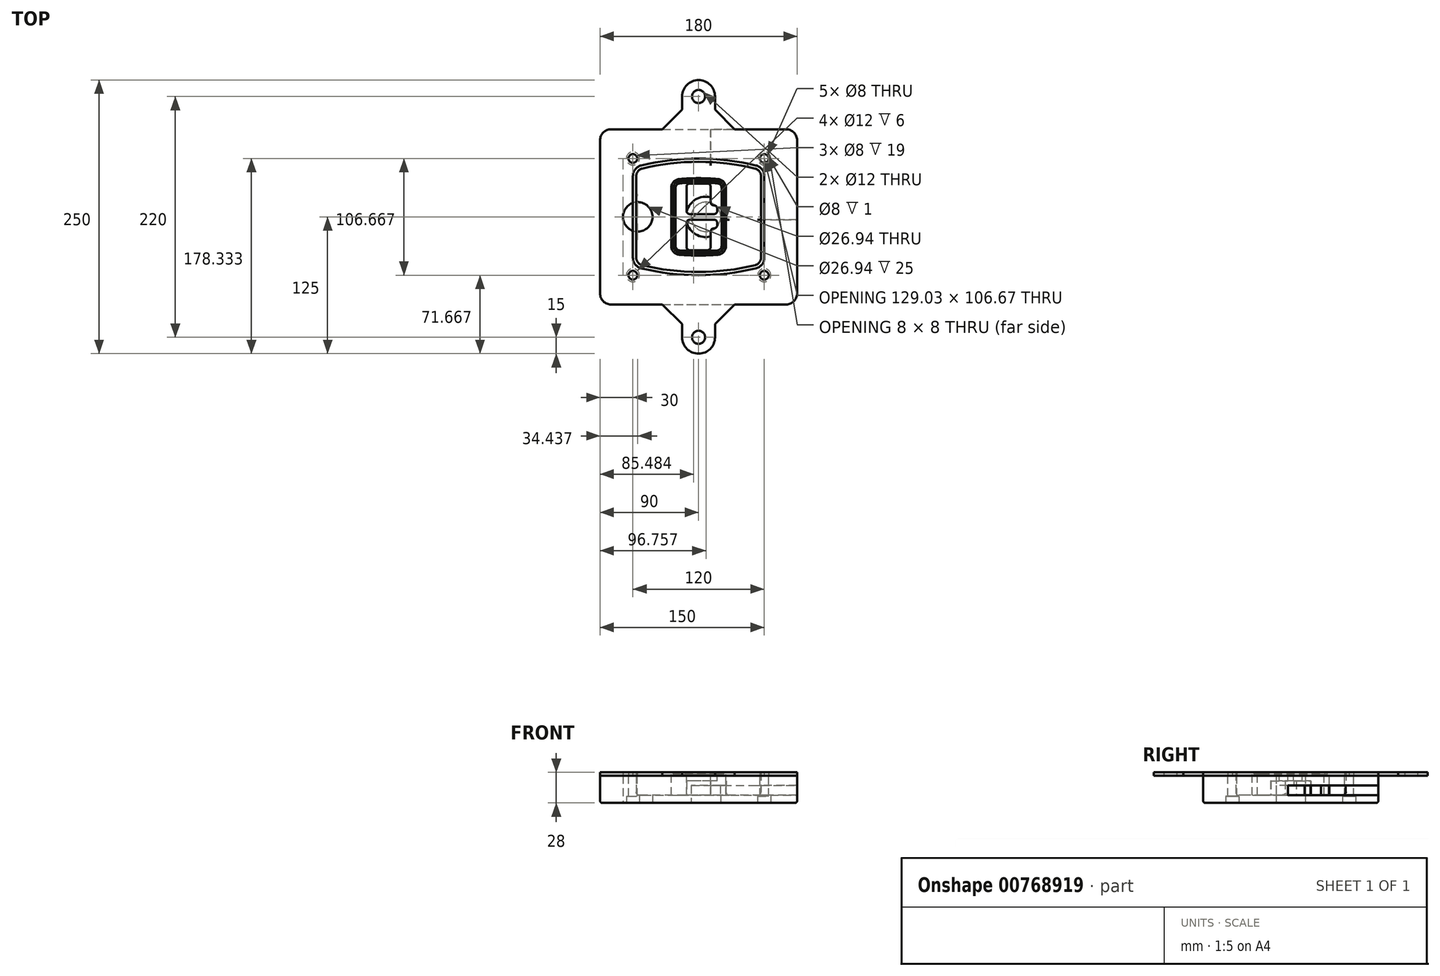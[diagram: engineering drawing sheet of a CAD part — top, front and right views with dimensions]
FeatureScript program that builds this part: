
annotation { "Feature Type Name" : "Feature", "Feature Type Description" : "" }
export const myFeature = defineFeature(function(context is Context, id is Id, definition is map)
    precondition{}
    {
        {
            var Q0;
            Q0=qCreatedBy(makeId("Top.planeOp"),FACE);
            var sketch = newSketch(context, id + "F0", { "sketchPlane" : qUnion([Q0])});
            skPoint(sketch, "E0.rect.middle", {"position": v(0, 0) * mm});
            skLineSegment(sketch, "E1.bottom", {"start": v(-80, -80) * mm, "end": v(80, -80) * mm});
            skLineSegment(sketch, "E1.top", {"start": v(-80, 80) * mm, "end": v(80, 80) * mm});
            skLineSegment(sketch, "E1.left", {"start": v(-90, -70) * mm, "end": v(-90, 70) * mm});
            skLineSegment(sketch, "E1.right", {"start": v(90, -70) * mm, "end": v(90, 70) * mm});
            skLineSegment(sketch, "E2", {"start": v(-90, 80) * mm, "end": v(90, -80) * mm, "construction": true});
            skLineSegment(sketch, "E3", {"start": v(90, 80) * mm, "end": v(-90, -80) * mm, "construction": true});
            skCircle(sketch, "E4", {"center": v(-60, 53.33) * mm, "radius": 4 * mm});
            skCircle(sketch, "E5", {"center": v(60, 53.33) * mm, "radius": 4 * mm});
            skCircle(sketch, "E6", {"center": v(60, -53.33) * mm, "radius": 4 * mm});
            skCircle(sketch, "E7", {"center": v(-60, -53.33) * mm, "radius": 4 * mm});
            skLineSegment(sketch, "E8", {"start": v(-60, 53.33) * mm, "end": v(60, 53.33) * mm, "construction": true});
            skLineSegment(sketch, "E9", {"start": v(60, 53.33) * mm, "end": v(60, -53.33) * mm, "construction": true});
            skLineSegment(sketch, "E10", {"start": v(60, -53.33) * mm, "end": v(-60, -53.33) * mm, "construction": true});
            skLineSegment(sketch, "E11", {"start": v(-60, -53.33) * mm, "end": v(-60, 53.33) * mm, "construction": true});
            skLineSegment(sketch, "E12", {"start": v(-60, 37.3) * mm, "end": v(-60, -37.3) * mm});
            skLineSegment(sketch, "E13", {"start": v(60, 37.3) * mm, "end": v(60, -37.3) * mm});
            skArc(sketch, "E14", {"start": v(52.38, 47.01) * mm, "mid": v(0, 53.33) * mm, "end": v(-52.38, 47.01) * mm});
            skArc(sketch, "E15", {"start": v(-52.38, -47.01) * mm, "mid": v(0, -53.33) * mm, "end": v(52.38, -47.01) * mm});
            skLineSegment(sketch, "E16", {"start": v(-60, 0) * mm, "end": v(60, 0) * mm, "construction": true});
            skPoint(sketch, "E17.visualSharp", {"position": v(-60, -45) * mm});
            skArc(sketch, "E17.filletArc", {"start": v(-60, -37.3) * mm, "mid": v(-57.87, -43.47) * mm, "end": v(-52.38, -47.01) * mm});
            skPoint(sketch, "E18.visualSharp", {"position": v(-60, 45) * mm});
            skArc(sketch, "E18.filletArc", {"start": v(-52.38, 47.01) * mm, "mid": v(-57.87, 43.47) * mm, "end": v(-60, 37.3) * mm});
            skPoint(sketch, "E19.visualSharp", {"position": v(60, 45) * mm});
            skArc(sketch, "E19.filletArc", {"start": v(60, 37.3) * mm, "mid": v(57.87, 43.47) * mm, "end": v(52.38, 47.01) * mm});
            skPoint(sketch, "E20.visualSharp", {"position": v(60, -45) * mm});
            skArc(sketch, "E20.filletArc", {"start": v(52.38, -47.01) * mm, "mid": v(57.87, -43.47) * mm, "end": v(60, -37.3) * mm});
            skPoint(sketch, "E21.visualSharp", {"position": v(-90, 80) * mm});
            skArc(sketch, "E21.filletArc", {"start": v(-80, 80) * mm, "mid": v(-87.07, 77.07) * mm, "end": v(-90, 70) * mm});
            skPoint(sketch, "E22.visualSharp", {"position": v(90, 80) * mm});
            skArc(sketch, "E22.filletArc", {"start": v(90, 70) * mm, "mid": v(87.07, 77.07) * mm, "end": v(80, 80) * mm});
            skPoint(sketch, "E23.visualSharp", {"position": v(90, -80) * mm});
            skArc(sketch, "E23.filletArc", {"start": v(80, -80) * mm, "mid": v(87.07, -77.07) * mm, "end": v(90, -70) * mm});
            skPoint(sketch, "E24.visualSharp", {"position": v(-90, -80) * mm});
            skArc(sketch, "E24.filletArc", {"start": v(-90, -70) * mm, "mid": v(-87.07, -77.07) * mm, "end": v(-80, -80) * mm});
            skArc(sketch, "E25.0", {"start": v(57, 37.3) * mm, "mid": v(55.5, 41.62) * mm, "end": v(51.67, 44.1) * mm});
            skLineSegment(sketch, "E25.1", {"start": v(57, 37.3) * mm, "end": v(57, -37.3) * mm});
            skArc(sketch, "E25.2", {"start": v(51.67, -44.1) * mm, "mid": v(55.5, -41.62) * mm, "end": v(57, -37.3) * mm});
            skArc(sketch, "E25.3", {"start": v(-51.67, -44.1) * mm, "mid": v(0, -50.33) * mm, "end": v(51.67, -44.1) * mm});
            skArc(sketch, "E25.4", {"start": v(-57, -37.3) * mm, "mid": v(-55.5, -41.62) * mm, "end": v(-51.67, -44.1) * mm});
            skArc(sketch, "E25.5", {"start": v(51.67, 44.1) * mm, "mid": v(0, 50.33) * mm, "end": v(-51.67, 44.1) * mm});
            skLineSegment(sketch, "E25.6", {"start": v(-57, 37.3) * mm, "end": v(-57, -37.3) * mm});
            skArc(sketch, "E25.7", {"start": v(-51.67, 44.1) * mm, "mid": v(-55.5, 41.62) * mm, "end": v(-57, 37.3) * mm});
            skArc(sketch, "E26.0", {"start": v(-53.33, 50.9) * mm, "mid": v(-61.01, 45.94) * mm, "end": v(-64, 37.3) * mm});
            skArc(sketch, "E26.1", {"start": v(53.33, 50.9) * mm, "mid": v(0, 57.33) * mm, "end": v(-53.33, 50.9) * mm});
            skArc(sketch, "E26.2", {"start": v(64, 37.3) * mm, "mid": v(61.01, 45.94) * mm, "end": v(53.33, 50.9) * mm});
            skLineSegment(sketch, "E26.3", {"start": v(64, 37.3) * mm, "end": v(64, -37.3) * mm});
            skArc(sketch, "E26.4", {"start": v(53.33, -50.9) * mm, "mid": v(61.01, -45.94) * mm, "end": v(64, -37.3) * mm});
            skLineSegment(sketch, "E26.5", {"start": v(-64, 37.3) * mm, "end": v(-64, -37.3) * mm});
            skArc(sketch, "E26.6", {"start": v(-53.33, -50.9) * mm, "mid": v(0, -57.33) * mm, "end": v(53.33, -50.9) * mm});
            skArc(sketch, "E26.7", {"start": v(-64, -37.3) * mm, "mid": v(-61.01, -45.94) * mm, "end": v(-53.33, -50.9) * mm});
            skSolve(sketch);
        }
        {
            var Q0;
            Q0=makeQuery(id+"F0.imprint","IMPRINT",FACE,{"disambiguationData":[TD([[makeQuery(id+"F0.imprint","IMPRINT",EDGE,{"derivedFrom":sQuery(id+"F0.wireOp",EDGE,"E1.bottom")}),1.0]])]});
            var Q1;
            Q1=makeQuery(id+"F0.imprint","IMPRINT",FACE,{"disambiguationData":[TD([[makeQuery(id+"F0.imprint","IMPRINT",EDGE,{"derivedFrom":sQuery(id+"F0.wireOp",EDGE,"E12")}),1.0]])]});
            var Q2;
            Q2=makeQuery(id+"F0.imprint","IMPRINT",FACE,{"disambiguationData":[TD([[makeQuery(id+"F0.imprint","IMPRINT",EDGE,{"derivedFrom":sQuery(id+"F0.wireOp",EDGE,"E25.0")}),1.0]])]});
            var Q3;
            Q3=makeQuery(id+"F0.imprint","IMPRINT",FACE,{"disambiguationData":[TD([[makeQuery(id+"F0.imprint","IMPRINT",EDGE,{"derivedFrom":sQuery(id+"F0.wireOp",EDGE,"E12")}),-1.0]])]});
            extrude(context, id + "F1", {"entities" : qUnion([Q0, Q1, Q2, Q3]), "oppositeDirection" : true, "depth" : 25 * mm});
        }
        {
            var Q0;
            Q0=makeQuery(id+"F0.imprint","IMPRINT",FACE,{"disambiguationData":[TD([[makeQuery(id+"F0.imprint","IMPRINT",EDGE,{"derivedFrom":sQuery(id+"F0.wireOp",EDGE,"E12")}),1.0]])]});
            extrude(context, id + "F2", {"entities" : qUnion([Q0]), "operationType" : NewBodyOperationType.ADD, "depth" : 3 * mm});
        }
        {
            var Q0;
            Q0=makeQuery(id+"F0.imprint","IMPRINT",FACE,{"disambiguationData":[TD([[makeQuery(id+"F0.imprint","IMPRINT",EDGE,{"derivedFrom":sQuery(id+"F0.wireOp",EDGE,"E25.0")}),1.0]])]});
            extrude(context, id + "F3", {"entities" : qUnion([Q0]), "operationType" : NewBodyOperationType.REMOVE, "oppositeDirection" : true, "depth" : 18 * mm});
        }
        {
            var Q0;
            Q0=makeQuery(id+"F2.opExtrude","CAP_FACE",FACE,{"disambiguationData":[OSD([sQuery(id+"F0.wireOp",EDGE,"E12"),sQuery(id+"F0.wireOp",EDGE,"E13"),sQuery(id+"F0.wireOp",EDGE,"E14"),sQuery(id+"F0.wireOp",EDGE,"E15"),sQuery(id+"F0.wireOp",EDGE,"E17.filletArc"),sQuery(id+"F0.wireOp",EDGE,"E18.filletArc"),sQuery(id+"F0.wireOp",EDGE,"E19.filletArc"),sQuery(id+"F0.wireOp",EDGE,"E20.filletArc"),sQuery(id+"F0.wireOp",EDGE,"E25.0"),sQuery(id+"F0.wireOp",EDGE,"E25.1"),sQuery(id+"F0.wireOp",EDGE,"E25.2"),sQuery(id+"F0.wireOp",EDGE,"E25.3"),sQuery(id+"F0.wireOp",EDGE,"E25.4"),sQuery(id+"F0.wireOp",EDGE,"E25.5"),sQuery(id+"F0.wireOp",EDGE,"E25.6"),sQuery(id+"F0.wireOp",EDGE,"E25.7")])],"isStart":false});
            var sketch = newSketch(context, id + "F4", { "sketchPlane" : qUnion([Q0])});
            skArc(sketch, "E27.0", {"start": v(-17.7, -34.56) * mm, "mid": v(0, -35.33) * mm, "end": v(17.7, -34.56) * mm});
            skArc(sketch, "E28.0", {"start": v(17.7, 34.56) * mm, "mid": v(0, 35.33) * mm, "end": v(-17.7, 34.56) * mm});
            skLineSegment(sketch, "E29", {"start": v(-25, 26.59) * mm, "end": v(-25, -26.59) * mm});
            skLineSegment(sketch, "E30", {"start": v(25, 26.59) * mm, "end": v(25, -26.59) * mm});
            skLineSegment(sketch, "E31", {"start": v(-25, 33.78) * mm, "end": v(25, 33.78) * mm, "construction": true});
            skLineSegment(sketch, "E32", {"start": v(-25, -33.78) * mm, "end": v(25, -33.78) * mm, "construction": true});
            skPoint(sketch, "E33.visualSharp", {"position": v(-25, 33.78) * mm});
            skArc(sketch, "E33.filletArc", {"start": v(-17.7, 34.56) * mm, "mid": v(-22.9, 32) * mm, "end": v(-25, 26.59) * mm});
            skPoint(sketch, "E34.visualSharp", {"position": v(25, 33.78) * mm});
            skArc(sketch, "E34.filletArc", {"start": v(25, 26.59) * mm, "mid": v(22.9, 32) * mm, "end": v(17.7, 34.56) * mm});
            skPoint(sketch, "E35.visualSharp", {"position": v(25, -33.78) * mm});
            skArc(sketch, "E35.filletArc", {"start": v(17.7, -34.56) * mm, "mid": v(22.9, -32) * mm, "end": v(25, -26.59) * mm});
            skPoint(sketch, "E36.visualSharp", {"position": v(-25, -33.78) * mm});
            skArc(sketch, "E36.filletArc", {"start": v(-25, -26.59) * mm, "mid": v(-22.9, -32) * mm, "end": v(-17.7, -34.56) * mm});
            skArc(sketch, "E37.0", {"start": v(51.67, 44.1) * mm, "mid": v(0, 50.33) * mm, "end": v(-51.67, 44.1) * mm});
            skArc(sketch, "E37.1", {"start": v(-51.67, 44.1) * mm, "mid": v(-55.5, 41.62) * mm, "end": v(-57, 37.3) * mm});
            skLineSegment(sketch, "E37.2", {"start": v(-57, 37.3) * mm, "end": v(-57, -37.3) * mm});
            skArc(sketch, "E37.3", {"start": v(-57, -37.3) * mm, "mid": v(-55.5, -41.62) * mm, "end": v(-51.67, -44.1) * mm});
            skArc(sketch, "E37.4", {"start": v(-51.67, -44.1) * mm, "mid": v(0, -50.33) * mm, "end": v(51.67, -44.1) * mm});
            skArc(sketch, "E37.5", {"start": v(51.67, -44.1) * mm, "mid": v(55.5, -41.62) * mm, "end": v(57, -37.3) * mm});
            skLineSegment(sketch, "E37.6", {"start": v(57, 37.3) * mm, "end": v(57, -37.3) * mm});
            skArc(sketch, "E37.7", {"start": v(57, 37.3) * mm, "mid": v(55.5, 41.62) * mm, "end": v(51.67, 44.1) * mm});
            skLineSegment(sketch, "E38.0", {"start": v(23, 26.59) * mm, "end": v(23, -26.59) * mm});
            skArc(sketch, "E38.1", {"start": v(17.53, -32.56) * mm, "mid": v(21.42, -30.64) * mm, "end": v(23, -26.59) * mm});
            skArc(sketch, "E38.2", {"start": v(-17.53, -32.56) * mm, "mid": v(0, -33.33) * mm, "end": v(17.53, -32.56) * mm});
            skArc(sketch, "E38.3", {"start": v(-23, -26.59) * mm, "mid": v(-21.42, -30.64) * mm, "end": v(-17.53, -32.56) * mm});
            skLineSegment(sketch, "E38.4", {"start": v(-23, 26.59) * mm, "end": v(-23, -26.59) * mm});
            skArc(sketch, "E38.5", {"start": v(23, 26.59) * mm, "mid": v(21.42, 30.64) * mm, "end": v(17.53, 32.56) * mm});
            skArc(sketch, "E38.6", {"start": v(-17.53, 32.56) * mm, "mid": v(-21.42, 30.64) * mm, "end": v(-23, 26.59) * mm});
            skArc(sketch, "E38.7", {"start": v(17.53, 32.56) * mm, "mid": v(0, 33.33) * mm, "end": v(-17.53, 32.56) * mm});
            skArc(sketch, "E39.0", {"start": v(21, 26.59) * mm, "mid": v(19.95, 29.29) * mm, "end": v(17.35, 30.57) * mm});
            skLineSegment(sketch, "E39.1", {"start": v(21, 26.59) * mm, "end": v(21, -26.59) * mm});
            skArc(sketch, "E39.2", {"start": v(17.35, -30.57) * mm, "mid": v(19.95, -29.29) * mm, "end": v(21, -26.59) * mm});
            skArc(sketch, "E39.3", {"start": v(-17.35, -30.57) * mm, "mid": v(0, -31.33) * mm, "end": v(17.35, -30.57) * mm});
            skArc(sketch, "E39.4", {"start": v(-21, -26.59) * mm, "mid": v(-19.95, -29.29) * mm, "end": v(-17.35, -30.57) * mm});
            skArc(sketch, "E39.5", {"start": v(17.35, 30.57) * mm, "mid": v(0, 31.33) * mm, "end": v(-17.35, 30.57) * mm});
            skLineSegment(sketch, "E39.6", {"start": v(-21, 26.59) * mm, "end": v(-21, -26.59) * mm});
            skArc(sketch, "E39.7", {"start": v(-17.35, 30.57) * mm, "mid": v(-19.95, 29.29) * mm, "end": v(-21, 26.59) * mm});
            skLineSegment(sketch, "E40", {"start": v(-25, 0) * mm, "end": v(25, 0) * mm, "construction": true});
            skLineSegment(sketch, "E41", {"start": v(-11, 5.5) * mm, "end": v(-11, 27.5) * mm});
            skLineSegment(sketch, "E42", {"start": v(-8, 30.5) * mm, "end": v(8, 30.5) * mm});
            skLineSegment(sketch, "E43", {"start": v(11, 27.5) * mm, "end": v(11, 13.5) * mm});
            skLineSegment(sketch, "E44", {"start": v(14, 10.5) * mm, "end": v(14, 10.5) * mm});
            skLineSegment(sketch, "E45", {"start": v(17, 7.5) * mm, "end": v(17, 5.5) * mm});
            skLineSegment(sketch, "E46", {"start": v(14, 2.5) * mm, "end": v(-8, 2.5) * mm});
            skPoint(sketch, "E47.visualSharp", {"position": v(-11, 30.5) * mm});
            skArc(sketch, "E47.filletArc", {"start": v(-8, 30.5) * mm, "mid": v(-10.12, 29.62) * mm, "end": v(-11, 27.5) * mm});
            skPoint(sketch, "E48.visualSharp", {"position": v(11, 30.5) * mm});
            skArc(sketch, "E48.filletArc", {"start": v(11, 27.5) * mm, "mid": v(10.12, 29.62) * mm, "end": v(8, 30.5) * mm});
            skPoint(sketch, "E49.visualSharp", {"position": v(11, 10.5) * mm});
            skArc(sketch, "E49.filletArc", {"start": v(11, 13.5) * mm, "mid": v(11.88, 11.38) * mm, "end": v(14, 10.5) * mm});
            skPoint(sketch, "E50.visualSharp", {"position": v(17, 10.5) * mm});
            skArc(sketch, "E50.filletArc", {"start": v(17, 7.5) * mm, "mid": v(16.12, 9.62) * mm, "end": v(14, 10.5) * mm});
            skPoint(sketch, "E51.visualSharp", {"position": v(17, 2.5) * mm});
            skArc(sketch, "E51.filletArc", {"start": v(14, 2.5) * mm, "mid": v(16.12, 3.38) * mm, "end": v(17, 5.5) * mm});
            skPoint(sketch, "E52.visualSharp", {"position": v(-11, 2.5) * mm});
            skArc(sketch, "E52.filletArc", {"start": v(-11, 5.5) * mm, "mid": v(-10.12, 3.38) * mm, "end": v(-8, 2.5) * mm});
            skLineSegment(sketch, "E53.0.MirrorCS", {"start": v(14, -2.5) * mm, "end": v(-8, -2.5) * mm});
            skArc(sketch, "E54.0.MirrorCS", {"start": v(-11, -5.5) * mm, "mid": v(-10.12, -3.38) * mm, "end": v(-8, -2.5) * mm});
            skLineSegment(sketch, "E55.0.MirrorCS", {"start": v(-11, -5.5) * mm, "end": v(-11, -27.5) * mm});
            skArc(sketch, "E56.0.MirrorCS", {"start": v(-8, -30.5) * mm, "mid": v(-10.12, -29.62) * mm, "end": v(-11, -27.5) * mm});
            skLineSegment(sketch, "E57.0.MirrorCS", {"start": v(-8, -30.5) * mm, "end": v(8, -30.5) * mm});
            skArc(sketch, "E58.0.MirrorCS", {"start": v(11, -27.5) * mm, "mid": v(10.12, -29.62) * mm, "end": v(8, -30.5) * mm});
            skLineSegment(sketch, "E59.0.MirrorCS", {"start": v(11, -27.5) * mm, "end": v(11, -13.5) * mm});
            skArc(sketch, "E60.0.MirrorCS", {"start": v(11, -13.5) * mm, "mid": v(11.88, -11.38) * mm, "end": v(14, -10.5) * mm});
            skArc(sketch, "E61.0.MirrorCS", {"start": v(17, -7.5) * mm, "mid": v(16.12, -9.62) * mm, "end": v(14, -10.5) * mm});
            skLineSegment(sketch, "E62.0.MirrorCS", {"start": v(17, -7.5) * mm, "end": v(17, -5.5) * mm});
            skArc(sketch, "E63.0.MirrorCS", {"start": v(14, -2.5) * mm, "mid": v(16.12, -3.38) * mm, "end": v(17, -5.5) * mm});
            skSolve(sketch);
        }
        {
            var Q0;
            Q0=makeQuery(id+"F4.imprint","IMPRINT",FACE,{"disambiguationData":[TD([[makeQuery(id+"F4.imprint","IMPRINT",EDGE,{"derivedFrom":sQuery(id+"F4.wireOp",EDGE,"E27.0")}),1.0]])]});
            var Q1;
            Q1=makeQuery(id+"F4.imprint","IMPRINT",FACE,{"disambiguationData":[TD([[makeQuery(id+"F4.imprint","IMPRINT",EDGE,{"derivedFrom":sQuery(id+"F4.wireOp",EDGE,"E38.0")}),-1.0]])]});
            var Q2;
            Q2=makeQuery(id+"F4.imprint","IMPRINT",FACE,{"disambiguationData":[TD([[makeQuery(id+"F4.imprint","IMPRINT",EDGE,{"derivedFrom":sQuery(id+"F4.wireOp",EDGE,"E39.0")}),1.0]])]});
            extrude(context, id + "F5", {"entities" : qUnion([Q0, Q1, Q2]), "operationType" : NewBodyOperationType.ADD, "endBound" : BoundingType.UP_TO_NEXT, "oppositeDirection" : true, "depth" : 25 * mm});
        }
        {
            var Q0;
            Q0=makeQuery(id+"F4.imprint","IMPRINT",FACE,{"disambiguationData":[TD([[makeQuery(id+"F4.imprint","IMPRINT",EDGE,{"derivedFrom":sQuery(id+"F4.wireOp",EDGE,"E38.0")}),-1.0]])]});
            extrude(context, id + "F6", {"entities" : qUnion([Q0]), "operationType" : NewBodyOperationType.REMOVE, "oppositeDirection" : true, "depth" : 2 * mm});
        }
        {
            var Q0;
            Q0=makeQuery(id+"F1.opExtrude","CAP_FACE",FACE,{"disambiguationData":[OSD([sQuery(id+"F0.wireOp",EDGE,"E1.bottom"),sQuery(id+"F0.wireOp",EDGE,"E1.top"),sQuery(id+"F0.wireOp",EDGE,"E1.left"),sQuery(id+"F0.wireOp",EDGE,"E1.right"),sQuery(id+"F0.wireOp",EDGE,"E4"),sQuery(id+"F0.wireOp",EDGE,"E5"),sQuery(id+"F0.wireOp",EDGE,"E6"),sQuery(id+"F0.wireOp",EDGE,"E7"),sQuery(id+"F0.wireOp",EDGE,"E21.filletArc"),sQuery(id+"F0.wireOp",EDGE,"E22.filletArc"),sQuery(id+"F0.wireOp",EDGE,"E23.filletArc"),sQuery(id+"F0.wireOp",EDGE,"E24.filletArc")])],"isStart":false});
            var sketch = newSketch(context, id + "F7", { "sketchPlane" : qUnion([Q0])});
            skCircle(sketch, "E64", {"center": v(6.76, 0) * mm, "radius": 13.47 * mm});
            skCircle(sketch, "E65", {"center": v(-55.56, 0) * mm, "radius": 13.47 * mm});
            skLineSegment(sketch, "E66", {"start": v(90, 0) * mm, "end": v(-90, 0) * mm});
            skCircle(sketch, "E67", {"center": v(6.76, 0) * mm, "radius": 18.47 * mm});
            skCircle(sketch, "E68", {"center": v(60, -53.33) * mm, "radius": 6 * mm});
            skCircle(sketch, "E69", {"center": v(-60, -53.33) * mm, "radius": 6 * mm});
            skCircle(sketch, "E70", {"center": v(-60, 53.33) * mm, "radius": 6 * mm});
            skCircle(sketch, "E71", {"center": v(60, 53.33) * mm, "radius": 6 * mm});
            skSolve(sketch);
        }
        {
            var Q0;
            {var subQ1=sQuery(id+"F7.wireOp",EDGE,"E66");var subQ4=sQuery(id+"F7.wireOp",EDGE,"E64");var subQ6=makeQuery(id+"F7.imprint","INTERSECT",VERTEX,{"disambiguationData":[OD(0.0)],"derivedFrom":[subQ4,subQ1]});Q0=makeQuery(id+"F7.imprint","IMPRINT",FACE,{"disambiguationData":[TD([[makeQuery(id+"F7.imprint","IMPRINT",EDGE,{"disambiguationData":[TD([[subQ6,-1.0]])],"derivedFrom":subQ4}),-1.0]])]});}
            var Q1;
            {var subQ0=sQuery(id+"F7.wireOp",EDGE,"E66");var subQ1=sQuery(id+"F7.wireOp",EDGE,"E64");var subQ3=makeQuery(id+"F7.imprint","INTERSECT",VERTEX,{"disambiguationData":[OD(0.0)],"derivedFrom":[subQ1,subQ0]});Q1=makeQuery(id+"F7.imprint","IMPRINT",FACE,{"disambiguationData":[TD([[makeQuery(id+"F7.imprint","IMPRINT",EDGE,{"disambiguationData":[TD([[subQ3,-1.0]])],"derivedFrom":subQ1}),1.0]])]});}
            var Q2;
            {var subQ0=sQuery(id+"F7.wireOp",EDGE,"E66");var subQ1=sQuery(id+"F7.wireOp",EDGE,"E64");var subQ3=makeQuery(id+"F7.imprint","INTERSECT",VERTEX,{"disambiguationData":[OD(0.0)],"derivedFrom":[subQ1,subQ0]});Q2=makeQuery(id+"F7.imprint","IMPRINT",FACE,{"disambiguationData":[TD([[makeQuery(id+"F7.imprint","IMPRINT",EDGE,{"disambiguationData":[TD([[subQ3,1.0]])],"derivedFrom":subQ1}),1.0]])]});}
            var Q3;
            {var subQ1=sQuery(id+"F7.wireOp",EDGE,"E66");var subQ4=sQuery(id+"F7.wireOp",EDGE,"E64");var subQ6=makeQuery(id+"F7.imprint","INTERSECT",VERTEX,{"disambiguationData":[OD(0.0)],"derivedFrom":[subQ4,subQ1]});Q3=makeQuery(id+"F7.imprint","IMPRINT",FACE,{"disambiguationData":[TD([[makeQuery(id+"F7.imprint","IMPRINT",EDGE,{"disambiguationData":[TD([[subQ6,1.0]])],"derivedFrom":subQ4}),-1.0]])]});}
            extrude(context, id + "F8", {"entities" : qUnion([Q0, Q1, Q2, Q3]), "operationType" : NewBodyOperationType.ADD, "oppositeDirection" : true, "depth" : 20 * mm});
        }
        {
            var Q0;
            {var subQ0=sQuery(id+"F7.wireOp",EDGE,"E66");var subQ1=sQuery(id+"F7.wireOp",EDGE,"E64");var subQ3=makeQuery(id+"F7.imprint","INTERSECT",VERTEX,{"disambiguationData":[OD(0.0)],"derivedFrom":[subQ1,subQ0]});Q0=makeQuery(id+"F7.imprint","IMPRINT",FACE,{"disambiguationData":[TD([[makeQuery(id+"F7.imprint","IMPRINT",EDGE,{"disambiguationData":[TD([[subQ3,-1.0]])],"derivedFrom":subQ1}),1.0]])]});}
            var Q1;
            {var subQ0=sQuery(id+"F7.wireOp",EDGE,"E66");var subQ1=sQuery(id+"F7.wireOp",EDGE,"E64");var subQ3=makeQuery(id+"F7.imprint","INTERSECT",VERTEX,{"disambiguationData":[OD(0.0)],"derivedFrom":[subQ1,subQ0]});Q1=makeQuery(id+"F7.imprint","IMPRINT",FACE,{"disambiguationData":[TD([[makeQuery(id+"F7.imprint","IMPRINT",EDGE,{"disambiguationData":[TD([[subQ3,1.0]])],"derivedFrom":subQ1}),1.0]])]});}
            extrude(context, id + "F9", {"entities" : qUnion([Q0, Q1]), "operationType" : NewBodyOperationType.REMOVE, "oppositeDirection" : true, "depth" : 16 * mm});
        }
        {
            var Q0;
            {var subQ0=sQuery(id+"F7.wireOp",EDGE,"E66");var subQ1=sQuery(id+"F7.wireOp",EDGE,"E65");var subQ3=makeQuery(id+"F7.imprint","INTERSECT",VERTEX,{"disambiguationData":[OD(0.0)],"derivedFrom":[subQ1,subQ0]});Q0=makeQuery(id+"F7.imprint","IMPRINT",FACE,{"disambiguationData":[TD([[makeQuery(id+"F7.imprint","IMPRINT",EDGE,{"disambiguationData":[TD([[subQ3,-1.0]])],"derivedFrom":subQ1}),1.0]])]});}
            var Q1;
            {var subQ0=sQuery(id+"F7.wireOp",EDGE,"E66");var subQ1=sQuery(id+"F7.wireOp",EDGE,"E65");var subQ3=makeQuery(id+"F7.imprint","INTERSECT",VERTEX,{"disambiguationData":[OD(0.0)],"derivedFrom":[subQ1,subQ0]});Q1=makeQuery(id+"F7.imprint","IMPRINT",FACE,{"disambiguationData":[TD([[makeQuery(id+"F7.imprint","IMPRINT",EDGE,{"disambiguationData":[TD([[subQ3,1.0]])],"derivedFrom":subQ1}),1.0]])]});}
            extrude(context, id + "F10", {"entities" : qUnion([Q0, Q1]), "operationType" : NewBodyOperationType.REMOVE, "oppositeDirection" : true, "depth" : 25 * mm});
        }
        {
            var Q0;
            Q0=makeQuery(id+"F7.imprint","IMPRINT",FACE,{"disambiguationData":[TD([[makeQuery(id+"F7.imprint","IMPRINT",EDGE,{"derivedFrom":sQuery(id+"F7.wireOp",EDGE,"E68")}),1.0]])]});
            var Q1;
            Q1=makeQuery(id+"F7.imprint","IMPRINT",FACE,{"disambiguationData":[TD([[makeQuery(id+"F7.imprint","IMPRINT",EDGE,{"derivedFrom":makeQuery(id+"F1.opExtrude","CAP_EDGE",EDGE,{"disambiguationData":[OSD([sQuery(id+"F0.wireOp",EDGE,"E5")])],"isStart":false})}),-1.0]])]});
            var Q2;
            Q2=makeQuery(id+"F7.imprint","IMPRINT",FACE,{"disambiguationData":[TD([[makeQuery(id+"F7.imprint","IMPRINT",EDGE,{"derivedFrom":sQuery(id+"F7.wireOp",EDGE,"E69")}),1.0]])]});
            var Q3;
            Q3=makeQuery(id+"F7.imprint","IMPRINT",FACE,{"disambiguationData":[TD([[makeQuery(id+"F7.imprint","IMPRINT",EDGE,{"derivedFrom":makeQuery(id+"F1.opExtrude","CAP_EDGE",EDGE,{"disambiguationData":[OSD([sQuery(id+"F0.wireOp",EDGE,"E4")])],"isStart":false})}),-1.0]])]});
            var Q4;
            Q4=makeQuery(id+"F7.imprint","IMPRINT",FACE,{"disambiguationData":[TD([[makeQuery(id+"F7.imprint","IMPRINT",EDGE,{"derivedFrom":sQuery(id+"F7.wireOp",EDGE,"E70")}),1.0]])]});
            var Q5;
            Q5=makeQuery(id+"F7.imprint","IMPRINT",FACE,{"disambiguationData":[TD([[makeQuery(id+"F7.imprint","IMPRINT",EDGE,{"derivedFrom":makeQuery(id+"F1.opExtrude","CAP_EDGE",EDGE,{"disambiguationData":[OSD([sQuery(id+"F0.wireOp",EDGE,"E7")])],"isStart":false})}),-1.0]])]});
            var Q6;
            Q6=makeQuery(id+"F7.imprint","IMPRINT",FACE,{"disambiguationData":[TD([[makeQuery(id+"F7.imprint","IMPRINT",EDGE,{"derivedFrom":sQuery(id+"F7.wireOp",EDGE,"E71")}),1.0]])]});
            var Q7;
            Q7=makeQuery(id+"F7.imprint","IMPRINT",FACE,{"disambiguationData":[TD([[makeQuery(id+"F7.imprint","IMPRINT",EDGE,{"derivedFrom":makeQuery(id+"F1.opExtrude","CAP_EDGE",EDGE,{"disambiguationData":[OSD([sQuery(id+"F0.wireOp",EDGE,"E6")])],"isStart":false})}),-1.0]])]});
            extrude(context, id + "F11", {"entities" : qUnion([Q0, Q1, Q2, Q3, Q4, Q5, Q6, Q7]), "operationType" : NewBodyOperationType.REMOVE, "oppositeDirection" : true, "depth" : 6 * mm});
        }
        {
            var Q0;
            Q0=makeQuery(id+"F9.boolean.opBoolean","COPY",FACE,{"derivedFrom":makeQuery(id+"F9.opExtrude","CAP_FACE",FACE,{"disambiguationData":[OSD([sQuery(id+"F7.wireOp",EDGE,"E64")])],"isStart":false})});
            var sketch = newSketch(context, id + "F12", { "sketchPlane" : qUnion([Q0])});
            skArc(sketch, "E72.0", {"start": v(11, -88.19) * mm, "mid": v(97.1, -83.6) * mm, "end": v(92.5, 2.5) * mm});
            skLineSegment(sketch, "E72.1", {"start": v(11, -17.97) * mm, "end": v(11, -17.97) * mm});
            skLineSegment(sketch, "E73", {"start": v(92.5, -105.13) * mm, "end": v(102.3, -105.13) * mm});
            skLineSegment(sketch, "E74.0", {"start": v(92.5, 2.5) * mm, "end": v(14, 2.5) * mm});
            skArc(sketch, "E74.1", {"start": v(14, 2.5) * mm, "mid": v(16.12, 3.38) * mm, "end": v(17, 5.5) * mm});
            skLineSegment(sketch, "E74.2", {"start": v(17, 7.5) * mm, "end": v(17, 5.5) * mm});
            skArc(sketch, "E74.3", {"start": v(17, 7.5) * mm, "mid": v(16.12, 9.62) * mm, "end": v(14, 10.5) * mm});
            skArc(sketch, "E74.4", {"start": v(11, 13.5) * mm, "mid": v(11.88, 11.38) * mm, "end": v(14, 10.5) * mm});
            skLineSegment(sketch, "E74.5", {"start": v(11, 13.5) * mm, "end": v(11, -88.19) * mm});
            skLineSegment(sketch, "E74.7", {"start": v(92.5, -2.5) * mm, "end": v(14, -2.5) * mm});
            skArc(sketch, "E74.8", {"start": v(14, -2.5) * mm, "mid": v(16.12, -3.38) * mm, "end": v(17, -5.5) * mm});
            skLineSegment(sketch, "E74.9", {"start": v(17, -7.5) * mm, "end": v(17, -5.5) * mm});
            skArc(sketch, "E74.10", {"start": v(17, -7.5) * mm, "mid": v(16.12, -9.62) * mm, "end": v(14, -10.5) * mm});
            skArc(sketch, "E74.11", {"start": v(11, -13.5) * mm, "mid": v(11.88, -11.38) * mm, "end": v(14, -10.5) * mm});
            skLineSegment(sketch, "E74.12", {"start": v(11, -17.97) * mm, "end": v(11, -13.5) * mm});
            skPoint(sketch, "E75.orphan", {"position": v(11, -27.5) * mm});
            skPoint(sketch, "E76.orphan", {"position": v(-8, -2.5) * mm});
            skPoint(sketch, "E77.orphan", {"position": v(-8, 2.5) * mm});
            skPoint(sketch, "E78.orphan", {"position": v(11, 27.5) * mm});
            skSolve(sketch);
        }
        {
            var Q0;
            {var subQ7=sQuery(id+"F12.wireOp",EDGE,"E72.0");var subQ14=sQuery(id+"F12.wireOp",EDGE,"E72.1");var subQ16=sQuery(id+"F12.wireOp",EDGE,"E74.1");var subQ18=sQuery(id+"F12.wireOp",EDGE,"E74.8");Q0=qUnion([makeQuery(id+"F12.imprint","IMPRINT",FACE,{"disambiguationData":[TD([[makeQuery(id+"F12.imprint","IMPRINT",EDGE,{"derivedFrom":subQ7}),1.0]])]}),makeQuery(id+"F12.imprint","IMPRINT",FACE,{"disambiguationData":[TD([[makeQuery(id+"F12.imprint","IMPRINT",EDGE,{"derivedFrom":subQ14}),1.0]])]}),makeQuery(id+"F12.imprint","IMPRINT",FACE,{"disambiguationData":[TD([[makeQuery(id+"F12.imprint","IMPRINT",EDGE,{"derivedFrom":subQ16}),1.0]])]}),makeQuery(id+"F12.imprint","IMPRINT",FACE,{"disambiguationData":[TD([[makeQuery(id+"F12.imprint","IMPRINT",EDGE,{"derivedFrom":subQ18}),-1.0]])]})]);}
            var Q1;
            Q1=makeQuery(id+"F5.boolean.opBoolean","SPLIT",FACE,{"disambiguationData":[TD([makeQuery(id+"F5.opExtrude","SWEPT_FACE",FACE,{"disambiguationData":[OSD([sQuery(id+"F4.wireOp",EDGE,"E41")])]})])],"derivedFrom":makeQuery(id+"F3.boolean.opBoolean","COPY",FACE,{"derivedFrom":makeQuery(id+"F3.opExtrude","CAP_FACE",FACE,{"disambiguationData":[OSD([sQuery(id+"F0.wireOp",EDGE,"E25.0"),sQuery(id+"F0.wireOp",EDGE,"E25.1"),sQuery(id+"F0.wireOp",EDGE,"E25.2"),sQuery(id+"F0.wireOp",EDGE,"E25.3"),sQuery(id+"F0.wireOp",EDGE,"E25.4"),sQuery(id+"F0.wireOp",EDGE,"E25.5"),sQuery(id+"F0.wireOp",EDGE,"E25.6"),sQuery(id+"F0.wireOp",EDGE,"E25.7")])],"isStart":false})})});
            extrude(context, id + "F13", {"entities" : qUnion([Q0]), "operationType" : NewBodyOperationType.REMOVE, "endBound" : BoundingType.UP_TO_SURFACE, "endBoundEntityFace" : qUnion([Q1]), "depth" : 25 * mm});
        }
        {
            var Q0;
            Q0=makeQuery(id+"F3.boolean.opBoolean","COPY",EDGE,{"derivedFrom":makeQuery(id+"F3.opExtrude","CAP_EDGE",EDGE,{"disambiguationData":[OSD([sQuery(id+"F0.wireOp",EDGE,"E25.6")])],"isStart":false})});
            var Q1;
            Q1=makeQuery(id+"F8.boolean.opBoolean","INTERSECT",EDGE,{"derivedFrom":[makeQuery(id+"F5.opExtrude","SWEPT_FACE",FACE,{"disambiguationData":[OSD([sQuery(id+"F4.wireOp",EDGE,"E30")])]}),makeQuery(id+"F8.opExtrude","CAP_FACE",FACE,{"disambiguationData":[OSD([sQuery(id+"F7.wireOp",EDGE,"E67")])],"isStart":false})]});
            var Q2;
            Q2=makeQuery(id+"F8.boolean.opBoolean","INTERSECT",EDGE,{"disambiguationData":[OD(1.0)],"derivedFrom":[makeQuery(id+"F5.opExtrude","SWEPT_FACE",FACE,{"disambiguationData":[OSD([sQuery(id+"F4.wireOp",EDGE,"E30")])]}),makeQuery(id+"F8.opExtrude","SWEPT_FACE",FACE,{"disambiguationData":[OSD([sQuery(id+"F7.wireOp",EDGE,"E67")])]})]});
            var Q3;
            {var subQ0=makeQuery(id+"F3.boolean.opBoolean","COPY",FACE,{"derivedFrom":makeQuery(id+"F3.opExtrude","CAP_FACE",FACE,{"disambiguationData":[OSD([sQuery(id+"F0.wireOp",EDGE,"E25.0"),sQuery(id+"F0.wireOp",EDGE,"E25.1"),sQuery(id+"F0.wireOp",EDGE,"E25.2"),sQuery(id+"F0.wireOp",EDGE,"E25.3"),sQuery(id+"F0.wireOp",EDGE,"E25.4"),sQuery(id+"F0.wireOp",EDGE,"E25.5"),sQuery(id+"F0.wireOp",EDGE,"E25.6"),sQuery(id+"F0.wireOp",EDGE,"E25.7")])],"isStart":false})});var subQ1=sQuery(id+"F4.wireOp",EDGE,"E30");Q3=makeQuery(id+"F8.boolean.opBoolean","SPLIT",EDGE,{"disambiguationData":[TD([makeQuery(id+"F5.opExtrude","SWEPT_FACE",FACE,{"disambiguationData":[OSD([sQuery(id+"F4.wireOp",EDGE,"E35.filletArc")])]})])],"derivedFrom":makeQuery(id+"F5.opExtrude","TWEAK_EDGE",EDGE,{"derivedFrom":[subQ0,makeQuery(id+"F4.imprint","IMPRINT",EDGE,{"derivedFrom":subQ1})]})});}
            var Q4;
            {var subQ0=sQuery(id+"F0.wireOp",EDGE,"E25.0");var subQ1=sQuery(id+"F0.wireOp",EDGE,"E25.1");var subQ2=sQuery(id+"F0.wireOp",EDGE,"E25.2");var subQ3=sQuery(id+"F0.wireOp",EDGE,"E25.3");var subQ4=sQuery(id+"F0.wireOp",EDGE,"E25.4");var subQ5=sQuery(id+"F0.wireOp",EDGE,"E25.5");var subQ6=sQuery(id+"F0.wireOp",EDGE,"E25.6");var subQ7=sQuery(id+"F0.wireOp",EDGE,"E25.7");Q4=makeQuery(id+"F8.boolean.opBoolean","INTERSECT",EDGE,{"derivedFrom":[makeQuery(id+"F5.boolean.opBoolean","SPLIT",FACE,{"disambiguationData":[TD([makeQuery(id+"F2.opExtrude","SWEPT_FACE",FACE,{"disambiguationData":[OSD([subQ0])]})])],"derivedFrom":makeQuery(id+"F3.boolean.opBoolean","COPY",FACE,{"derivedFrom":makeQuery(id+"F3.opExtrude","CAP_FACE",FACE,{"disambiguationData":[OSD([subQ0,subQ1,subQ2,subQ3,subQ4,subQ5,subQ6,subQ7])],"isStart":false})})}),makeQuery(id+"F8.opExtrude","SWEPT_FACE",FACE,{"disambiguationData":[OSD([sQuery(id+"F7.wireOp",EDGE,"E67")])]})]});}
            var Q5;
            Q5=makeQuery(id+"F8.boolean.opBoolean","INTERSECT",EDGE,{"disambiguationData":[OD(0.0)],"derivedFrom":[makeQuery(id+"F5.opExtrude","SWEPT_FACE",FACE,{"disambiguationData":[OSD([sQuery(id+"F4.wireOp",EDGE,"E30")])]}),makeQuery(id+"F8.opExtrude","SWEPT_FACE",FACE,{"disambiguationData":[OSD([sQuery(id+"F7.wireOp",EDGE,"E67")])]})]});
            fillet(context, id + "F14", {"entities" : qUnion([Q0, Q1, Q2, Q3, Q4, Q5]), "radius" : 3 * mm, "tangentPropagation" : true, "allowEdgeOverflow" : false});
        }
        {
            var Q0;
            Q0=makeQuery(id+"F1.opExtrude","CAP_EDGE",EDGE,{"disambiguationData":[OSD([sQuery(id+"F0.wireOp",EDGE,"E1.bottom")])],"isStart":false});
            fillet(context, id + "F15", {"entities" : qUnion([Q0]), "radius" : 2 * mm, "tangentPropagation" : true, "allowEdgeOverflow" : false});
        }
        {
            var Q0;
            {var subQ0=sQuery(id+"F0.wireOp",EDGE,"E21.filletArc");var subQ1=sQuery(id+"F0.wireOp",EDGE,"E7");var subQ2=sQuery(id+"F0.wireOp",EDGE,"E6");var subQ3=sQuery(id+"F0.wireOp",EDGE,"E5");var subQ4=sQuery(id+"F0.wireOp",EDGE,"E4");var subQ5=sQuery(id+"F0.wireOp",EDGE,"E22.filletArc");var subQ6=sQuery(id+"F0.wireOp",EDGE,"E1.bottom");var subQ7=sQuery(id+"F0.wireOp",EDGE,"E1.right");var subQ8=sQuery(id+"F0.wireOp",EDGE,"E1.top");var subQ9=sQuery(id+"F0.wireOp",EDGE,"E1.left");var subQ10=sQuery(id+"F0.wireOp",EDGE,"E23.filletArc");var subQ11=sQuery(id+"F0.wireOp",EDGE,"E24.filletArc");Q0=makeQuery(id+"F2.boolean.opBoolean","SPLIT",FACE,{"disambiguationData":[TD([makeQuery(id+"F1.opExtrude","SWEPT_FACE",FACE,{"disambiguationData":[OSD([subQ6])]})])],"derivedFrom":makeQuery(id+"F1.opExtrude","CAP_FACE",FACE,{"disambiguationData":[OSD([subQ6,subQ8,subQ9,subQ7,subQ4,subQ3,subQ2,subQ1,subQ0,subQ5,subQ10,subQ11])],"isStart":true})});}
            var sketch = newSketch(context, id + "F16", { "sketchPlane" : qUnion([Q0])});
            skLineSegment(sketch, "E79", {"start": v(0, 80) * mm, "end": v(0, 110) * mm, "construction": true});
            skCircle(sketch, "E80", {"center": v(0, 110) * mm, "radius": 6 * mm});
            skArc(sketch, "E81", {"start": v(-15, 110) * mm, "mid": v(0, 125) * mm, "end": v(15, 110) * mm});
            skLineSegment(sketch, "E82", {"start": v(-15, 110) * mm, "end": v(-15, 98) * mm});
            skLineSegment(sketch, "E83", {"start": v(15, 110) * mm, "end": v(15, 98) * mm});
            skLineSegment(sketch, "E84", {"start": v(15, 98) * mm, "end": v(33, 80) * mm});
            skLineSegment(sketch, "E85", {"start": v(-15, 98) * mm, "end": v(-33, 80) * mm});
            skLineSegment(sketch, "E86", {"start": v(-90, 0) * mm, "end": v(90, 0) * mm, "construction": true});
            skLineSegment(sketch, "E87.MirrorCS", {"start": v(-15, -110) * mm, "end": v(-15, -98) * mm});
            skCircle(sketch, "E88.MirrorC", {"center": v(0, -110) * mm, "radius": 6 * mm});
            skLineSegment(sketch, "E89.MirrorCS", {"start": v(15, -110) * mm, "end": v(15, -98) * mm});
            skLineSegment(sketch, "E90.MirrorCS", {"start": v(15, -98) * mm, "end": v(33, -80) * mm});
            skLineSegment(sketch, "E91.MirrorCS", {"start": v(-15, -98) * mm, "end": v(-33, -80) * mm});
            skArc(sketch, "E92.MirrorCS", {"start": v(-15, -110) * mm, "mid": v(0, -125) * mm, "end": v(15, -110) * mm});
            skLineSegment(sketch, "E93.MirrorCS", {"start": v(0, -80) * mm, "end": v(0, -110) * mm, "construction": true});
            skSolve(sketch);
        }
        {
            var Q0;
            Q0=makeQuery(id+"F16.imprint","IMPRINT",FACE,{"disambiguationData":[TD([[makeQuery(id+"F16.imprint","IMPRINT",EDGE,{"derivedFrom":sQuery(id+"F16.wireOp",EDGE,"E80")}),-1.0]])]});
            var Q1;
            Q1=makeQuery(id+"F16.imprint","IMPRINT",FACE,{"disambiguationData":[TD([[makeQuery(id+"F16.imprint","IMPRINT",EDGE,{"derivedFrom":makeQuery(id+"F1.opExtrude","CAP_EDGE",EDGE,{"disambiguationData":[OSD([sQuery(id+"F0.wireOp",EDGE,"E1.left")])],"isStart":true})}),-1.0]])]});
            var Q2;
            Q2=makeQuery(id+"F16.imprint","IMPRINT",FACE,{"disambiguationData":[TD([[makeQuery(id+"F16.imprint","IMPRINT",EDGE,{"derivedFrom":sQuery(id+"F16.wireOp",EDGE,"E87.MirrorCS")}),-1.0]])]});
            var Q3;
            Q3=makeQuery(id+"F2.opExtrude","CAP_FACE",FACE,{"disambiguationData":[OSD([sQuery(id+"F0.wireOp",EDGE,"E12"),sQuery(id+"F0.wireOp",EDGE,"E13"),sQuery(id+"F0.wireOp",EDGE,"E14"),sQuery(id+"F0.wireOp",EDGE,"E15"),sQuery(id+"F0.wireOp",EDGE,"E17.filletArc"),sQuery(id+"F0.wireOp",EDGE,"E18.filletArc"),sQuery(id+"F0.wireOp",EDGE,"E19.filletArc"),sQuery(id+"F0.wireOp",EDGE,"E20.filletArc"),sQuery(id+"F0.wireOp",EDGE,"E25.0"),sQuery(id+"F0.wireOp",EDGE,"E25.1"),sQuery(id+"F0.wireOp",EDGE,"E25.2"),sQuery(id+"F0.wireOp",EDGE,"E25.3"),sQuery(id+"F0.wireOp",EDGE,"E25.4"),sQuery(id+"F0.wireOp",EDGE,"E25.5"),sQuery(id+"F0.wireOp",EDGE,"E25.6"),sQuery(id+"F0.wireOp",EDGE,"E25.7")])],"isStart":false});
            extrude(context, id + "F17", {"entities" : qUnion([Q0, Q1, Q2]), "endBound" : BoundingType.UP_TO_SURFACE, "depth" : 25 * mm, "endBoundEntityFace" : qUnion([Q3]), "offsetDistance" : 25 * mm});
        }
    });
